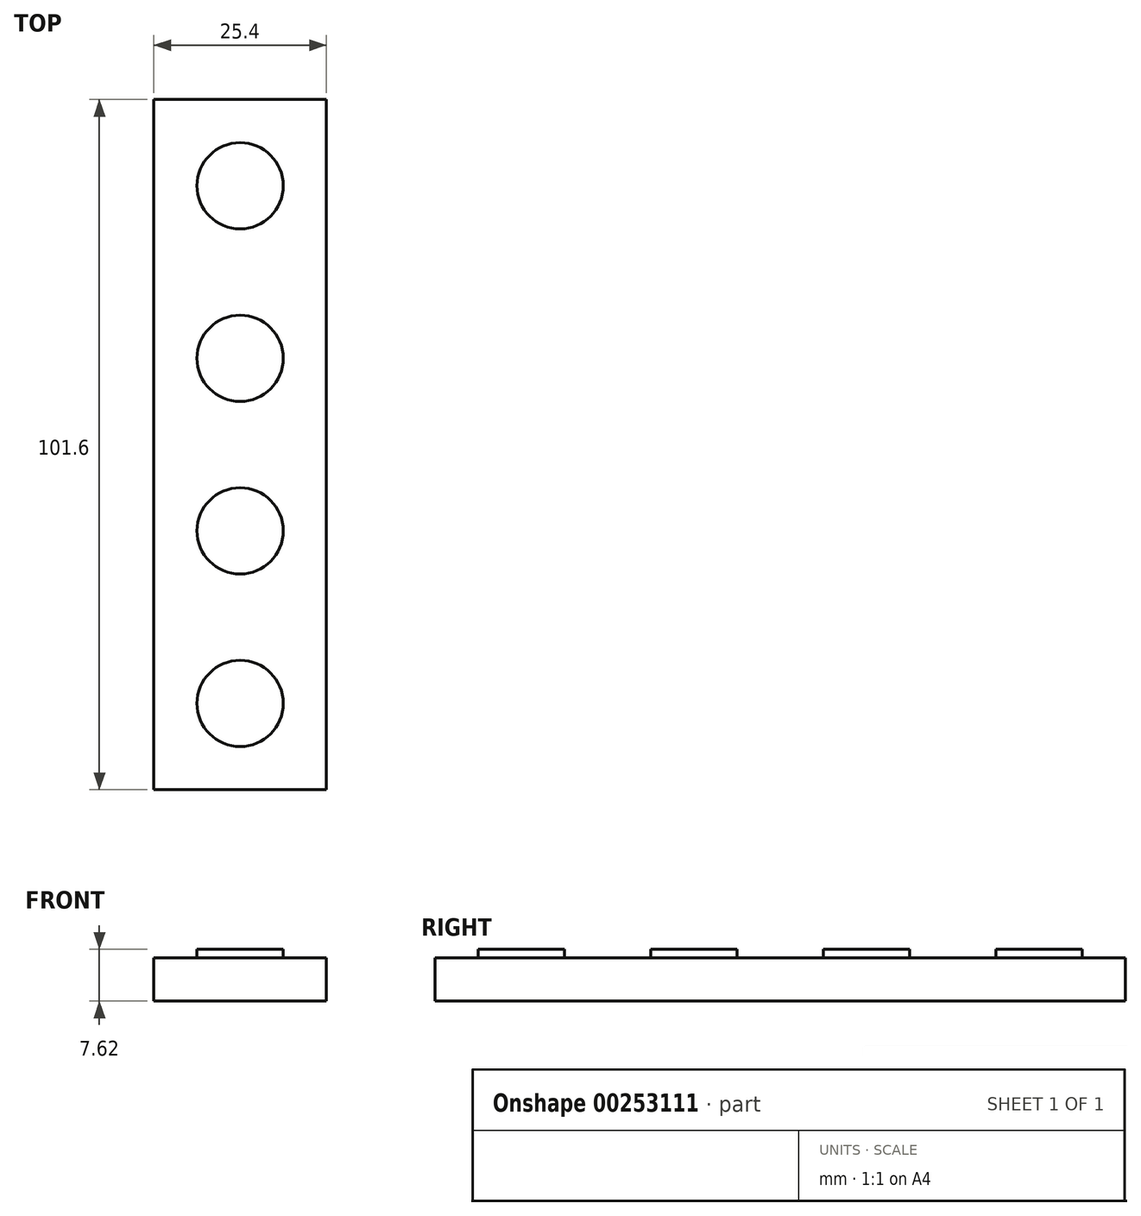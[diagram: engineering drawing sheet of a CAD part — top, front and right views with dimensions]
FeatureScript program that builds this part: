
annotation { "Feature Type Name" : "Feature", "Feature Type Description" : "" }
export const myFeature = defineFeature(function(context is Context, id is Id, definition is map)
    precondition{}
    {
        {
            var Q0;
            Q0=qCreatedBy(makeId("Top.planeOp"),FACE);
            var sketch = newSketch(context, id + "F0", { "sketchPlane" : qUnion([Q0])});
            skLineSegment(sketch, "E0.bottom", {"start": v(9.31, 45.04) * mm, "end": v(34.71, 45.04) * mm});
            skLineSegment(sketch, "E0.top", {"start": v(9.31, -56.56) * mm, "end": v(34.71, -56.56) * mm});
            skLineSegment(sketch, "E0.left", {"start": v(9.31, 45.04) * mm, "end": v(9.31, -56.56) * mm});
            skLineSegment(sketch, "E0.right", {"start": v(34.71, 45.04) * mm, "end": v(34.71, -56.56) * mm});
            skLineSegment(sketch, "E1", {"start": v(9.31, 45.04) * mm, "end": v(9.31, 32.34) * mm});
            skLineSegment(sketch, "E2", {"start": v(9.31, 32.34) * mm, "end": v(9.31, 6.94) * mm});
            skLineSegment(sketch, "E3", {"start": v(9.31, -56.56) * mm, "end": v(9.31, -43.86) * mm});
            skLineSegment(sketch, "E4", {"start": v(9.31, -18.46) * mm, "end": v(9.31, -43.86) * mm});
            skCircle(sketch, "E5", {"center": v(22.01, 32.34) * mm, "radius": 6.35 * mm});
            skPoint(sketch, "E5.centerSnap0", {"position": v(22.01, 45.04) * mm});
            skCircle(sketch, "E6", {"center": v(22.01, 6.94) * mm, "radius": 6.35 * mm});
            skCircle(sketch, "E7", {"center": v(22.01, -18.46) * mm, "radius": 6.35 * mm});
            skCircle(sketch, "E8", {"center": v(22.01, -43.86) * mm, "radius": 6.35 * mm});
            skSolve(sketch);
        }
        {
            var Q0;
            Q0 = qSketchRegion(id + "F0", true);
            extrude(context, id + "F1", {"entities" : qUnion([Q0]), "depth" : 6.35 * mm});
        }
        {
            var Q0;
            Q0=makeQuery(id+"F0.imprint","IMPRINT",FACE,{"disambiguationData":[TD([[makeQuery(id+"F0.imprint","IMPRINT",EDGE,{"derivedFrom":sQuery(id+"F0.wireOp",EDGE,"E7")}),1.0]])]});
            var Q1;
            Q1=makeQuery(id+"F0.imprint","IMPRINT",FACE,{"disambiguationData":[TD([[makeQuery(id+"F0.imprint","IMPRINT",EDGE,{"derivedFrom":sQuery(id+"F0.wireOp",EDGE,"E8")}),1.0]])]});
            var Q2;
            Q2=makeQuery(id+"F0.imprint","IMPRINT",FACE,{"disambiguationData":[TD([[makeQuery(id+"F0.imprint","IMPRINT",EDGE,{"derivedFrom":sQuery(id+"F0.wireOp",EDGE,"E6")}),1.0]])]});
            var Q3;
            Q3=makeQuery(id+"F0.imprint","IMPRINT",FACE,{"disambiguationData":[TD([[makeQuery(id+"F0.imprint","IMPRINT",EDGE,{"derivedFrom":sQuery(id+"F0.wireOp",EDGE,"E5")}),1.0]])]});
            extrude(context, id + "F2", {"entities" : qUnion([Q0, Q1, Q2, Q3]), "operationType" : NewBodyOperationType.ADD, "depth" : 7.62 * mm});
        }
    });
